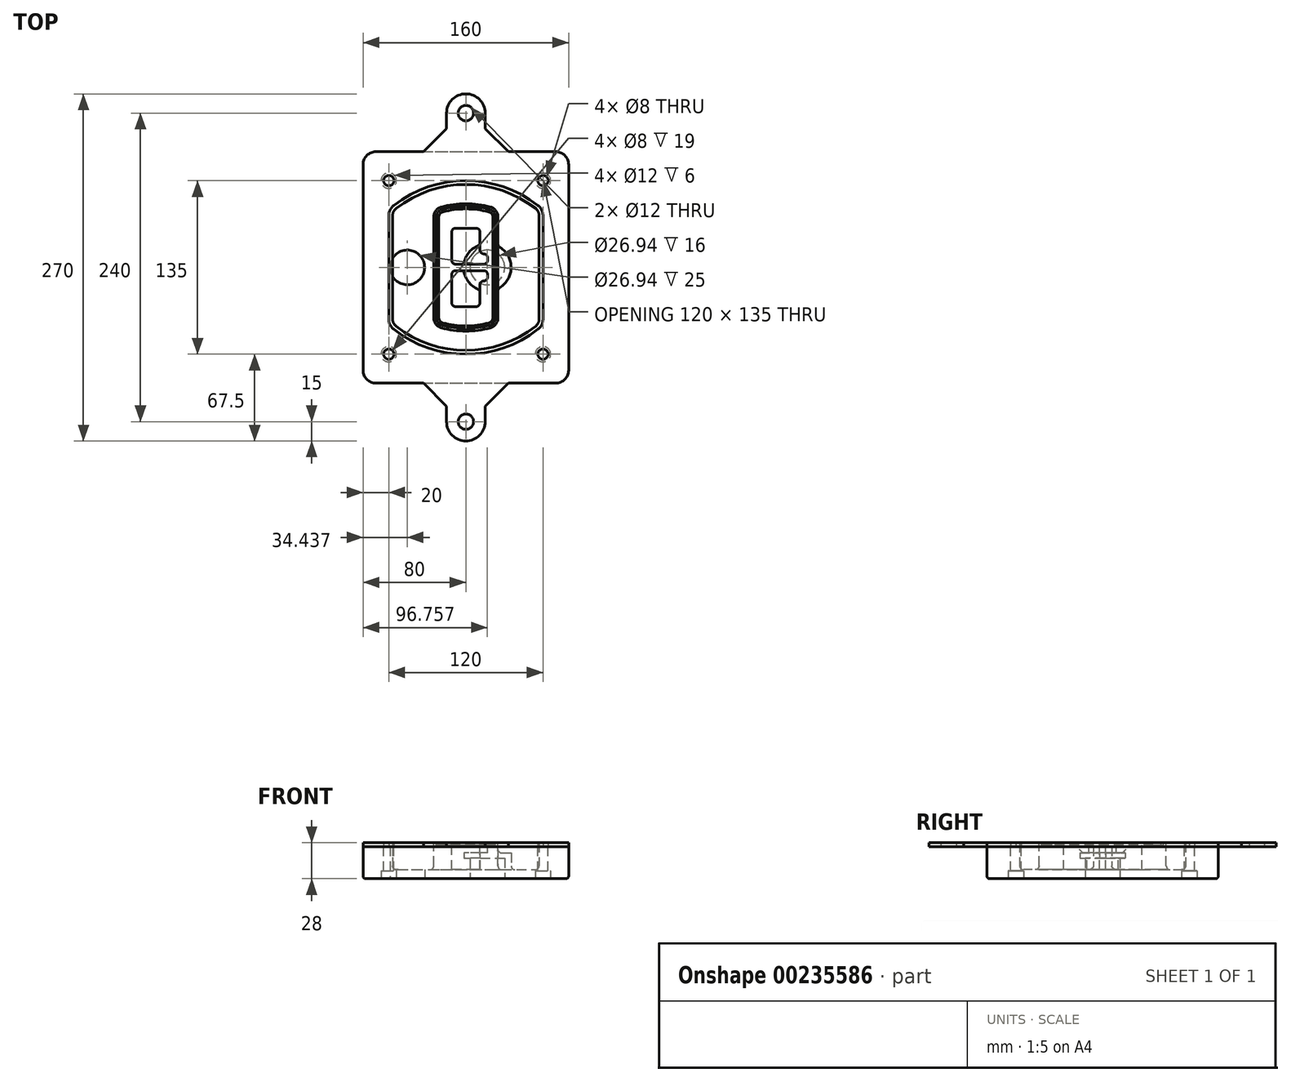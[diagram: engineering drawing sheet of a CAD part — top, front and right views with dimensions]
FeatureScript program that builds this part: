
annotation { "Feature Type Name" : "Feature", "Feature Type Description" : "" }
export const myFeature = defineFeature(function(context is Context, id is Id, definition is map)
    precondition{}
    {
        {
            var Q0;
            Q0=qCreatedBy(makeId("Top.planeOp"),FACE);
            var sketch = newSketch(context, id + "F0", { "sketchPlane" : qUnion([Q0])});
            skPoint(sketch, "E0.rect.middle", {"position": v(0, 0) * mm});
            skLineSegment(sketch, "E1.bottom", {"start": v(-70, -90) * mm, "end": v(70, -90) * mm});
            skLineSegment(sketch, "E1.top", {"start": v(-70, 90) * mm, "end": v(70, 90) * mm});
            skLineSegment(sketch, "E1.left", {"start": v(-80, -80) * mm, "end": v(-80, 80) * mm});
            skLineSegment(sketch, "E1.right", {"start": v(80, -80) * mm, "end": v(80, 80) * mm});
            skLineSegment(sketch, "E2", {"start": v(-80, 90) * mm, "end": v(80, -90) * mm, "construction": true});
            skLineSegment(sketch, "E3", {"start": v(80, 90) * mm, "end": v(-80, -90) * mm, "construction": true});
            skCircle(sketch, "E4", {"center": v(-60, 67.5) * mm, "radius": 4 * mm});
            skCircle(sketch, "E5", {"center": v(60, 67.5) * mm, "radius": 4 * mm});
            skCircle(sketch, "E6", {"center": v(60, -67.5) * mm, "radius": 4 * mm});
            skCircle(sketch, "E7", {"center": v(-60, -67.5) * mm, "radius": 4 * mm});
            skLineSegment(sketch, "E8", {"start": v(-60, 67.5) * mm, "end": v(60, 67.5) * mm, "construction": true});
            skLineSegment(sketch, "E9", {"start": v(60, 67.5) * mm, "end": v(60, -67.5) * mm, "construction": true});
            skLineSegment(sketch, "E10", {"start": v(60, -67.5) * mm, "end": v(-60, -67.5) * mm, "construction": true});
            skLineSegment(sketch, "E11", {"start": v(-60, -67.5) * mm, "end": v(-60, 67.5) * mm, "construction": true});
            skLineSegment(sketch, "E12", {"start": v(-60, 40.3) * mm, "end": v(-60, -40.3) * mm});
            skLineSegment(sketch, "E13", {"start": v(60, 40.3) * mm, "end": v(60, -40.3) * mm});
            skArc(sketch, "E14", {"start": v(56.15, 48.18) * mm, "mid": v(0, 67.5) * mm, "end": v(-56.15, 48.18) * mm});
            skArc(sketch, "E15", {"start": v(-56.15, -48.18) * mm, "mid": v(0, -67.5) * mm, "end": v(56.15, -48.18) * mm});
            skLineSegment(sketch, "E16", {"start": v(-60, 0) * mm, "end": v(60, 0) * mm, "construction": true});
            skPoint(sketch, "E17.visualSharp", {"position": v(-60, -45) * mm});
            skArc(sketch, "E17.filletArc", {"start": v(-60, -40.3) * mm, "mid": v(-58.99, -44.68) * mm, "end": v(-56.15, -48.18) * mm});
            skPoint(sketch, "E18.visualSharp", {"position": v(-60, 45) * mm});
            skArc(sketch, "E18.filletArc", {"start": v(-56.15, 48.18) * mm, "mid": v(-58.99, 44.68) * mm, "end": v(-60, 40.3) * mm});
            skPoint(sketch, "E19.visualSharp", {"position": v(60, 45) * mm});
            skArc(sketch, "E19.filletArc", {"start": v(60, 40.3) * mm, "mid": v(58.99, 44.68) * mm, "end": v(56.15, 48.18) * mm});
            skPoint(sketch, "E20.visualSharp", {"position": v(60, -45) * mm});
            skArc(sketch, "E20.filletArc", {"start": v(56.15, -48.18) * mm, "mid": v(58.99, -44.68) * mm, "end": v(60, -40.3) * mm});
            skPoint(sketch, "E21.visualSharp", {"position": v(-80, 90) * mm});
            skArc(sketch, "E21.filletArc", {"start": v(-70, 90) * mm, "mid": v(-77.07, 87.07) * mm, "end": v(-80, 80) * mm});
            skPoint(sketch, "E22.visualSharp", {"position": v(80, 90) * mm});
            skArc(sketch, "E22.filletArc", {"start": v(80, 80) * mm, "mid": v(77.07, 87.07) * mm, "end": v(70, 90) * mm});
            skPoint(sketch, "E23.visualSharp", {"position": v(80, -90) * mm});
            skArc(sketch, "E23.filletArc", {"start": v(70, -90) * mm, "mid": v(77.07, -87.07) * mm, "end": v(80, -80) * mm});
            skPoint(sketch, "E24.visualSharp", {"position": v(-80, -90) * mm});
            skArc(sketch, "E24.filletArc", {"start": v(-80, -80) * mm, "mid": v(-77.07, -87.07) * mm, "end": v(-70, -90) * mm});
            skArc(sketch, "E25.0", {"start": v(57, 40.3) * mm, "mid": v(56.3, 43.36) * mm, "end": v(54.3, 45.81) * mm});
            skLineSegment(sketch, "E25.1", {"start": v(57, 40.3) * mm, "end": v(57, -40.3) * mm});
            skArc(sketch, "E25.2", {"start": v(54.3, -45.81) * mm, "mid": v(56.3, -43.36) * mm, "end": v(57, -40.3) * mm});
            skArc(sketch, "E25.3", {"start": v(-54.3, -45.81) * mm, "mid": v(0, -64.5) * mm, "end": v(54.3, -45.81) * mm});
            skArc(sketch, "E25.4", {"start": v(-57, -40.3) * mm, "mid": v(-56.3, -43.36) * mm, "end": v(-54.3, -45.81) * mm});
            skArc(sketch, "E25.5", {"start": v(54.3, 45.81) * mm, "mid": v(0, 64.5) * mm, "end": v(-54.3, 45.81) * mm});
            skLineSegment(sketch, "E25.6", {"start": v(-57, 40.3) * mm, "end": v(-57, -40.3) * mm});
            skArc(sketch, "E25.7", {"start": v(-54.3, 45.81) * mm, "mid": v(-56.3, 43.36) * mm, "end": v(-57, 40.3) * mm});
            skArc(sketch, "E26.0", {"start": v(-58.62, 51.33) * mm, "mid": v(-62.58, 46.43) * mm, "end": v(-64, 40.3) * mm});
            skArc(sketch, "E26.1", {"start": v(58.62, 51.33) * mm, "mid": v(0, 71.5) * mm, "end": v(-58.62, 51.33) * mm});
            skArc(sketch, "E26.2", {"start": v(64, 40.3) * mm, "mid": v(62.58, 46.43) * mm, "end": v(58.62, 51.33) * mm});
            skLineSegment(sketch, "E26.3", {"start": v(64, 40.3) * mm, "end": v(64, -40.3) * mm});
            skArc(sketch, "E26.4", {"start": v(58.62, -51.33) * mm, "mid": v(62.58, -46.43) * mm, "end": v(64, -40.3) * mm});
            skLineSegment(sketch, "E26.5", {"start": v(-64, 40.3) * mm, "end": v(-64, -40.3) * mm});
            skArc(sketch, "E26.6", {"start": v(-58.62, -51.33) * mm, "mid": v(0, -71.5) * mm, "end": v(58.62, -51.33) * mm});
            skArc(sketch, "E26.7", {"start": v(-64, -40.3) * mm, "mid": v(-62.58, -46.43) * mm, "end": v(-58.62, -51.33) * mm});
            skSolve(sketch);
        }
        {
            var Q0;
            Q0=makeQuery(id+"F0.imprint","IMPRINT",FACE,{"disambiguationData":[TD([[makeQuery(id+"F0.imprint","IMPRINT",EDGE,{"derivedFrom":sQuery(id+"F0.wireOp",EDGE,"E1.bottom")}),1.0]])]});
            var Q1;
            Q1=makeQuery(id+"F0.imprint","IMPRINT",FACE,{"disambiguationData":[TD([[makeQuery(id+"F0.imprint","IMPRINT",EDGE,{"derivedFrom":sQuery(id+"F0.wireOp",EDGE,"E12")}),1.0]])]});
            var Q2;
            Q2=makeQuery(id+"F0.imprint","IMPRINT",FACE,{"disambiguationData":[TD([[makeQuery(id+"F0.imprint","IMPRINT",EDGE,{"derivedFrom":sQuery(id+"F0.wireOp",EDGE,"E25.0")}),1.0]])]});
            var Q3;
            Q3=makeQuery(id+"F0.imprint","IMPRINT",FACE,{"disambiguationData":[TD([[makeQuery(id+"F0.imprint","IMPRINT",EDGE,{"derivedFrom":sQuery(id+"F0.wireOp",EDGE,"E12")}),-1.0]])]});
            extrude(context, id + "F1", {"entities" : qUnion([Q0, Q1, Q2, Q3]), "oppositeDirection" : true, "depth" : 25 * mm});
        }
        {
            var Q0;
            Q0=makeQuery(id+"F0.imprint","IMPRINT",FACE,{"disambiguationData":[TD([[makeQuery(id+"F0.imprint","IMPRINT",EDGE,{"derivedFrom":sQuery(id+"F0.wireOp",EDGE,"E12")}),1.0]])]});
            extrude(context, id + "F2", {"entities" : qUnion([Q0]), "operationType" : NewBodyOperationType.ADD, "depth" : 3 * mm});
        }
        {
            var Q0;
            Q0=makeQuery(id+"F0.imprint","IMPRINT",FACE,{"disambiguationData":[TD([[makeQuery(id+"F0.imprint","IMPRINT",EDGE,{"derivedFrom":sQuery(id+"F0.wireOp",EDGE,"E25.0")}),1.0]])]});
            extrude(context, id + "F3", {"entities" : qUnion([Q0]), "operationType" : NewBodyOperationType.REMOVE, "oppositeDirection" : true, "depth" : 18 * mm});
        }
        {
            var Q0;
            Q0=makeQuery(id+"F2.opExtrude","CAP_FACE",FACE,{"disambiguationData":[OSD([sQuery(id+"F0.wireOp",EDGE,"E12"),sQuery(id+"F0.wireOp",EDGE,"E13"),sQuery(id+"F0.wireOp",EDGE,"E14"),sQuery(id+"F0.wireOp",EDGE,"E15"),sQuery(id+"F0.wireOp",EDGE,"E17.filletArc"),sQuery(id+"F0.wireOp",EDGE,"E18.filletArc"),sQuery(id+"F0.wireOp",EDGE,"E19.filletArc"),sQuery(id+"F0.wireOp",EDGE,"E20.filletArc"),sQuery(id+"F0.wireOp",EDGE,"E25.0"),sQuery(id+"F0.wireOp",EDGE,"E25.1"),sQuery(id+"F0.wireOp",EDGE,"E25.2"),sQuery(id+"F0.wireOp",EDGE,"E25.3"),sQuery(id+"F0.wireOp",EDGE,"E25.4"),sQuery(id+"F0.wireOp",EDGE,"E25.5"),sQuery(id+"F0.wireOp",EDGE,"E25.6"),sQuery(id+"F0.wireOp",EDGE,"E25.7")])],"isStart":false});
            var sketch = newSketch(context, id + "F4", { "sketchPlane" : qUnion([Q0])});
            skArc(sketch, "E27.0", {"start": v(-19.08, -46.97) * mm, "mid": v(0, -49.5) * mm, "end": v(19.08, -46.97) * mm});
            skArc(sketch, "E28.0", {"start": v(19.08, 46.97) * mm, "mid": v(0, 49.5) * mm, "end": v(-19.08, 46.97) * mm});
            skLineSegment(sketch, "E29", {"start": v(-25, 39.25) * mm, "end": v(-25, -39.25) * mm});
            skLineSegment(sketch, "E30", {"start": v(25, 39.25) * mm, "end": v(25, -39.25) * mm});
            skLineSegment(sketch, "E31", {"start": v(-25, 45.1) * mm, "end": v(25, 45.1) * mm, "construction": true});
            skLineSegment(sketch, "E32", {"start": v(-25, -45.1) * mm, "end": v(25, -45.1) * mm, "construction": true});
            skPoint(sketch, "E33.visualSharp", {"position": v(-25, 45.1) * mm});
            skArc(sketch, "E33.filletArc", {"start": v(-19.08, 46.97) * mm, "mid": v(-23.35, 44.11) * mm, "end": v(-25, 39.25) * mm});
            skPoint(sketch, "E34.visualSharp", {"position": v(25, 45.1) * mm});
            skArc(sketch, "E34.filletArc", {"start": v(25, 39.25) * mm, "mid": v(23.35, 44.11) * mm, "end": v(19.08, 46.97) * mm});
            skPoint(sketch, "E35.visualSharp", {"position": v(25, -45.1) * mm});
            skArc(sketch, "E35.filletArc", {"start": v(19.08, -46.97) * mm, "mid": v(23.35, -44.11) * mm, "end": v(25, -39.25) * mm});
            skPoint(sketch, "E36.visualSharp", {"position": v(-25, -45.1) * mm});
            skArc(sketch, "E36.filletArc", {"start": v(-25, -39.25) * mm, "mid": v(-23.35, -44.11) * mm, "end": v(-19.08, -46.97) * mm});
            skArc(sketch, "E37.0", {"start": v(54.3, 45.81) * mm, "mid": v(0, 64.5) * mm, "end": v(-54.3, 45.81) * mm});
            skArc(sketch, "E37.1", {"start": v(-54.3, 45.81) * mm, "mid": v(-56.3, 43.36) * mm, "end": v(-57, 40.3) * mm});
            skLineSegment(sketch, "E37.2", {"start": v(-57, 40.3) * mm, "end": v(-57, -40.3) * mm});
            skArc(sketch, "E37.3", {"start": v(-57, -40.3) * mm, "mid": v(-56.3, -43.36) * mm, "end": v(-54.3, -45.81) * mm});
            skArc(sketch, "E37.4", {"start": v(-54.3, -45.81) * mm, "mid": v(0, -64.5) * mm, "end": v(54.3, -45.81) * mm});
            skArc(sketch, "E37.5", {"start": v(54.3, -45.81) * mm, "mid": v(56.3, -43.36) * mm, "end": v(57, -40.3) * mm});
            skLineSegment(sketch, "E37.6", {"start": v(57, 40.3) * mm, "end": v(57, -40.3) * mm});
            skArc(sketch, "E37.7", {"start": v(57, 40.3) * mm, "mid": v(56.3, 43.36) * mm, "end": v(54.3, 45.81) * mm});
            skLineSegment(sketch, "E38.0", {"start": v(23, 39.25) * mm, "end": v(23, -39.25) * mm});
            skArc(sketch, "E38.1", {"start": v(18.56, -45.04) * mm, "mid": v(21.76, -42.9) * mm, "end": v(23, -39.25) * mm});
            skArc(sketch, "E38.2", {"start": v(-18.56, -45.04) * mm, "mid": v(0, -47.5) * mm, "end": v(18.56, -45.04) * mm});
            skArc(sketch, "E38.3", {"start": v(-23, -39.25) * mm, "mid": v(-21.76, -42.9) * mm, "end": v(-18.56, -45.04) * mm});
            skLineSegment(sketch, "E38.4", {"start": v(-23, 39.25) * mm, "end": v(-23, -39.25) * mm});
            skArc(sketch, "E38.5", {"start": v(23, 39.25) * mm, "mid": v(21.76, 42.9) * mm, "end": v(18.56, 45.04) * mm});
            skArc(sketch, "E38.6", {"start": v(-18.56, 45.04) * mm, "mid": v(-21.76, 42.9) * mm, "end": v(-23, 39.25) * mm});
            skArc(sketch, "E38.7", {"start": v(18.56, 45.04) * mm, "mid": v(0, 47.5) * mm, "end": v(-18.56, 45.04) * mm});
            skArc(sketch, "E39.0", {"start": v(21, 39.25) * mm, "mid": v(20.18, 41.68) * mm, "end": v(18.04, 43.1) * mm});
            skLineSegment(sketch, "E39.1", {"start": v(21, 39.25) * mm, "end": v(21, -39.25) * mm});
            skArc(sketch, "E39.2", {"start": v(18.04, -43.1) * mm, "mid": v(20.18, -41.68) * mm, "end": v(21, -39.25) * mm});
            skArc(sketch, "E39.3", {"start": v(-18.04, -43.1) * mm, "mid": v(0, -45.5) * mm, "end": v(18.04, -43.1) * mm});
            skArc(sketch, "E39.4", {"start": v(-21, -39.25) * mm, "mid": v(-20.18, -41.68) * mm, "end": v(-18.04, -43.1) * mm});
            skArc(sketch, "E39.5", {"start": v(18.04, 43.1) * mm, "mid": v(0, 45.5) * mm, "end": v(-18.04, 43.1) * mm});
            skLineSegment(sketch, "E39.6", {"start": v(-21, 39.25) * mm, "end": v(-21, -39.25) * mm});
            skArc(sketch, "E39.7", {"start": v(-18.04, 43.1) * mm, "mid": v(-20.18, 41.68) * mm, "end": v(-21, 39.25) * mm});
            skLineSegment(sketch, "E40", {"start": v(-25, 0) * mm, "end": v(25, 0) * mm, "construction": true});
            skLineSegment(sketch, "E41", {"start": v(-11, 5.5) * mm, "end": v(-11, 27.5) * mm});
            skLineSegment(sketch, "E42", {"start": v(-8, 30.5) * mm, "end": v(8, 30.5) * mm});
            skLineSegment(sketch, "E43", {"start": v(11, 27.5) * mm, "end": v(11, 13.5) * mm});
            skLineSegment(sketch, "E44", {"start": v(14, 10.5) * mm, "end": v(14, 10.5) * mm});
            skLineSegment(sketch, "E45", {"start": v(17, 7.5) * mm, "end": v(17, 5.5) * mm});
            skLineSegment(sketch, "E46", {"start": v(14, 2.5) * mm, "end": v(-8, 2.5) * mm});
            skPoint(sketch, "E47.visualSharp", {"position": v(-11, 30.5) * mm});
            skArc(sketch, "E47.filletArc", {"start": v(-8, 30.5) * mm, "mid": v(-10.12, 29.62) * mm, "end": v(-11, 27.5) * mm});
            skPoint(sketch, "E48.visualSharp", {"position": v(11, 30.5) * mm});
            skArc(sketch, "E48.filletArc", {"start": v(11, 27.5) * mm, "mid": v(10.12, 29.62) * mm, "end": v(8, 30.5) * mm});
            skPoint(sketch, "E49.visualSharp", {"position": v(11, 10.5) * mm});
            skArc(sketch, "E49.filletArc", {"start": v(11, 13.5) * mm, "mid": v(11.88, 11.38) * mm, "end": v(14, 10.5) * mm});
            skPoint(sketch, "E50.visualSharp", {"position": v(17, 10.5) * mm});
            skArc(sketch, "E50.filletArc", {"start": v(17, 7.5) * mm, "mid": v(16.12, 9.62) * mm, "end": v(14, 10.5) * mm});
            skPoint(sketch, "E51.visualSharp", {"position": v(17, 2.5) * mm});
            skArc(sketch, "E51.filletArc", {"start": v(14, 2.5) * mm, "mid": v(16.12, 3.38) * mm, "end": v(17, 5.5) * mm});
            skPoint(sketch, "E52.visualSharp", {"position": v(-11, 2.5) * mm});
            skArc(sketch, "E52.filletArc", {"start": v(-11, 5.5) * mm, "mid": v(-10.12, 3.38) * mm, "end": v(-8, 2.5) * mm});
            skLineSegment(sketch, "E53.0.MirrorCS", {"start": v(14, -2.5) * mm, "end": v(-8, -2.5) * mm});
            skArc(sketch, "E54.0.MirrorCS", {"start": v(-11, -5.5) * mm, "mid": v(-10.12, -3.38) * mm, "end": v(-8, -2.5) * mm});
            skLineSegment(sketch, "E55.0.MirrorCS", {"start": v(-11, -5.5) * mm, "end": v(-11, -27.5) * mm});
            skArc(sketch, "E56.0.MirrorCS", {"start": v(-8, -30.5) * mm, "mid": v(-10.12, -29.62) * mm, "end": v(-11, -27.5) * mm});
            skLineSegment(sketch, "E57.0.MirrorCS", {"start": v(-8, -30.5) * mm, "end": v(8, -30.5) * mm});
            skArc(sketch, "E58.0.MirrorCS", {"start": v(11, -27.5) * mm, "mid": v(10.12, -29.62) * mm, "end": v(8, -30.5) * mm});
            skLineSegment(sketch, "E59.0.MirrorCS", {"start": v(11, -27.5) * mm, "end": v(11, -13.5) * mm});
            skArc(sketch, "E60.0.MirrorCS", {"start": v(11, -13.5) * mm, "mid": v(11.88, -11.38) * mm, "end": v(14, -10.5) * mm});
            skArc(sketch, "E61.0.MirrorCS", {"start": v(17, -7.5) * mm, "mid": v(16.12, -9.62) * mm, "end": v(14, -10.5) * mm});
            skLineSegment(sketch, "E62.0.MirrorCS", {"start": v(17, -7.5) * mm, "end": v(17, -5.5) * mm});
            skArc(sketch, "E63.0.MirrorCS", {"start": v(14, -2.5) * mm, "mid": v(16.12, -3.38) * mm, "end": v(17, -5.5) * mm});
            skSolve(sketch);
        }
        {
            var Q0;
            Q0=makeQuery(id+"F4.imprint","IMPRINT",FACE,{"disambiguationData":[TD([[makeQuery(id+"F4.imprint","IMPRINT",EDGE,{"derivedFrom":sQuery(id+"F4.wireOp",EDGE,"E27.0")}),1.0]])]});
            var Q1;
            Q1=makeQuery(id+"F4.imprint","IMPRINT",FACE,{"disambiguationData":[TD([[makeQuery(id+"F4.imprint","IMPRINT",EDGE,{"derivedFrom":sQuery(id+"F4.wireOp",EDGE,"E38.0")}),-1.0]])]});
            var Q2;
            Q2=makeQuery(id+"F4.imprint","IMPRINT",FACE,{"disambiguationData":[TD([[makeQuery(id+"F4.imprint","IMPRINT",EDGE,{"derivedFrom":sQuery(id+"F4.wireOp",EDGE,"E39.0")}),1.0]])]});
            extrude(context, id + "F5", {"entities" : qUnion([Q0, Q1, Q2]), "operationType" : NewBodyOperationType.ADD, "endBound" : BoundingType.UP_TO_NEXT, "oppositeDirection" : true, "depth" : 25 * mm});
        }
        {
            var Q0;
            Q0=makeQuery(id+"F4.imprint","IMPRINT",FACE,{"disambiguationData":[TD([[makeQuery(id+"F4.imprint","IMPRINT",EDGE,{"derivedFrom":sQuery(id+"F4.wireOp",EDGE,"E38.0")}),-1.0]])]});
            extrude(context, id + "F6", {"entities" : qUnion([Q0]), "operationType" : NewBodyOperationType.REMOVE, "oppositeDirection" : true, "depth" : 2 * mm});
        }
        {
            var Q0;
            Q0=makeQuery(id+"F1.opExtrude","CAP_FACE",FACE,{"disambiguationData":[OSD([sQuery(id+"F0.wireOp",EDGE,"E1.bottom"),sQuery(id+"F0.wireOp",EDGE,"E1.top"),sQuery(id+"F0.wireOp",EDGE,"E1.left"),sQuery(id+"F0.wireOp",EDGE,"E1.right"),sQuery(id+"F0.wireOp",EDGE,"E4"),sQuery(id+"F0.wireOp",EDGE,"E5"),sQuery(id+"F0.wireOp",EDGE,"E6"),sQuery(id+"F0.wireOp",EDGE,"E7"),sQuery(id+"F0.wireOp",EDGE,"E21.filletArc"),sQuery(id+"F0.wireOp",EDGE,"E22.filletArc"),sQuery(id+"F0.wireOp",EDGE,"E23.filletArc"),sQuery(id+"F0.wireOp",EDGE,"E24.filletArc")])],"isStart":false});
            var sketch = newSketch(context, id + "F7", { "sketchPlane" : qUnion([Q0])});
            skCircle(sketch, "E64", {"center": v(16.76, 0) * mm, "radius": 13.47 * mm});
            skCircle(sketch, "E65", {"center": v(-45.56, 0) * mm, "radius": 13.47 * mm});
            skLineSegment(sketch, "E66", {"start": v(80, 0) * mm, "end": v(-80, 0) * mm});
            skCircle(sketch, "E67", {"center": v(16.76, 0) * mm, "radius": 18.47 * mm});
            skCircle(sketch, "E68", {"center": v(60, -67.5) * mm, "radius": 6 * mm});
            skCircle(sketch, "E69", {"center": v(-60, -67.5) * mm, "radius": 6 * mm});
            skCircle(sketch, "E70", {"center": v(-60, 67.5) * mm, "radius": 6 * mm});
            skCircle(sketch, "E71", {"center": v(60, 67.5) * mm, "radius": 6 * mm});
            skSolve(sketch);
        }
        {
            var Q0;
            {var subQ1=sQuery(id+"F7.wireOp",EDGE,"E66");var subQ4=sQuery(id+"F7.wireOp",EDGE,"E64");var subQ6=makeQuery(id+"F7.imprint","INTERSECT",VERTEX,{"disambiguationData":[OD(0.0)],"derivedFrom":[subQ4,subQ1]});Q0=makeQuery(id+"F7.imprint","IMPRINT",FACE,{"disambiguationData":[TD([[makeQuery(id+"F7.imprint","IMPRINT",EDGE,{"disambiguationData":[TD([[subQ6,-1.0]])],"derivedFrom":subQ4}),-1.0]])]});}
            var Q1;
            {var subQ0=sQuery(id+"F7.wireOp",EDGE,"E66");var subQ1=sQuery(id+"F7.wireOp",EDGE,"E64");var subQ3=makeQuery(id+"F7.imprint","INTERSECT",VERTEX,{"disambiguationData":[OD(0.0)],"derivedFrom":[subQ1,subQ0]});Q1=makeQuery(id+"F7.imprint","IMPRINT",FACE,{"disambiguationData":[TD([[makeQuery(id+"F7.imprint","IMPRINT",EDGE,{"disambiguationData":[TD([[subQ3,-1.0]])],"derivedFrom":subQ1}),1.0]])]});}
            var Q2;
            {var subQ0=sQuery(id+"F7.wireOp",EDGE,"E66");var subQ1=sQuery(id+"F7.wireOp",EDGE,"E64");var subQ3=makeQuery(id+"F7.imprint","INTERSECT",VERTEX,{"disambiguationData":[OD(0.0)],"derivedFrom":[subQ1,subQ0]});Q2=makeQuery(id+"F7.imprint","IMPRINT",FACE,{"disambiguationData":[TD([[makeQuery(id+"F7.imprint","IMPRINT",EDGE,{"disambiguationData":[TD([[subQ3,1.0]])],"derivedFrom":subQ1}),1.0]])]});}
            var Q3;
            {var subQ1=sQuery(id+"F7.wireOp",EDGE,"E66");var subQ4=sQuery(id+"F7.wireOp",EDGE,"E64");var subQ6=makeQuery(id+"F7.imprint","INTERSECT",VERTEX,{"disambiguationData":[OD(0.0)],"derivedFrom":[subQ4,subQ1]});Q3=makeQuery(id+"F7.imprint","IMPRINT",FACE,{"disambiguationData":[TD([[makeQuery(id+"F7.imprint","IMPRINT",EDGE,{"disambiguationData":[TD([[subQ6,1.0]])],"derivedFrom":subQ4}),-1.0]])]});}
            extrude(context, id + "F8", {"entities" : qUnion([Q0, Q1, Q2, Q3]), "operationType" : NewBodyOperationType.ADD, "oppositeDirection" : true, "depth" : 20 * mm});
        }
        {
            var Q0;
            {var subQ0=sQuery(id+"F7.wireOp",EDGE,"E66");var subQ1=sQuery(id+"F7.wireOp",EDGE,"E64");var subQ3=makeQuery(id+"F7.imprint","INTERSECT",VERTEX,{"disambiguationData":[OD(0.0)],"derivedFrom":[subQ1,subQ0]});Q0=makeQuery(id+"F7.imprint","IMPRINT",FACE,{"disambiguationData":[TD([[makeQuery(id+"F7.imprint","IMPRINT",EDGE,{"disambiguationData":[TD([[subQ3,-1.0]])],"derivedFrom":subQ1}),1.0]])]});}
            var Q1;
            {var subQ0=sQuery(id+"F7.wireOp",EDGE,"E66");var subQ1=sQuery(id+"F7.wireOp",EDGE,"E64");var subQ3=makeQuery(id+"F7.imprint","INTERSECT",VERTEX,{"disambiguationData":[OD(0.0)],"derivedFrom":[subQ1,subQ0]});Q1=makeQuery(id+"F7.imprint","IMPRINT",FACE,{"disambiguationData":[TD([[makeQuery(id+"F7.imprint","IMPRINT",EDGE,{"disambiguationData":[TD([[subQ3,1.0]])],"derivedFrom":subQ1}),1.0]])]});}
            extrude(context, id + "F9", {"entities" : qUnion([Q0, Q1]), "operationType" : NewBodyOperationType.REMOVE, "oppositeDirection" : true, "depth" : 16 * mm});
        }
        {
            var Q0;
            {var subQ0=sQuery(id+"F7.wireOp",EDGE,"E66");var subQ1=sQuery(id+"F7.wireOp",EDGE,"E65");var subQ3=makeQuery(id+"F7.imprint","INTERSECT",VERTEX,{"disambiguationData":[OD(0.0)],"derivedFrom":[subQ1,subQ0]});Q0=makeQuery(id+"F7.imprint","IMPRINT",FACE,{"disambiguationData":[TD([[makeQuery(id+"F7.imprint","IMPRINT",EDGE,{"disambiguationData":[TD([[subQ3,-1.0]])],"derivedFrom":subQ1}),1.0]])]});}
            var Q1;
            {var subQ0=sQuery(id+"F7.wireOp",EDGE,"E66");var subQ1=sQuery(id+"F7.wireOp",EDGE,"E65");var subQ3=makeQuery(id+"F7.imprint","INTERSECT",VERTEX,{"disambiguationData":[OD(0.0)],"derivedFrom":[subQ1,subQ0]});Q1=makeQuery(id+"F7.imprint","IMPRINT",FACE,{"disambiguationData":[TD([[makeQuery(id+"F7.imprint","IMPRINT",EDGE,{"disambiguationData":[TD([[subQ3,1.0]])],"derivedFrom":subQ1}),1.0]])]});}
            extrude(context, id + "F10", {"entities" : qUnion([Q0, Q1]), "operationType" : NewBodyOperationType.REMOVE, "oppositeDirection" : true, "depth" : 25 * mm});
        }
        {
            var Q0;
            Q0=makeQuery(id+"F7.imprint","IMPRINT",FACE,{"disambiguationData":[TD([[makeQuery(id+"F7.imprint","IMPRINT",EDGE,{"derivedFrom":sQuery(id+"F7.wireOp",EDGE,"E68")}),1.0]])]});
            var Q1;
            Q1=makeQuery(id+"F7.imprint","IMPRINT",FACE,{"disambiguationData":[TD([[makeQuery(id+"F7.imprint","IMPRINT",EDGE,{"derivedFrom":makeQuery(id+"F1.opExtrude","CAP_EDGE",EDGE,{"disambiguationData":[OSD([sQuery(id+"F0.wireOp",EDGE,"E5")])],"isStart":false})}),-1.0]])]});
            var Q2;
            Q2=makeQuery(id+"F7.imprint","IMPRINT",FACE,{"disambiguationData":[TD([[makeQuery(id+"F7.imprint","IMPRINT",EDGE,{"derivedFrom":sQuery(id+"F7.wireOp",EDGE,"E69")}),1.0]])]});
            var Q3;
            Q3=makeQuery(id+"F7.imprint","IMPRINT",FACE,{"disambiguationData":[TD([[makeQuery(id+"F7.imprint","IMPRINT",EDGE,{"derivedFrom":makeQuery(id+"F1.opExtrude","CAP_EDGE",EDGE,{"disambiguationData":[OSD([sQuery(id+"F0.wireOp",EDGE,"E4")])],"isStart":false})}),-1.0]])]});
            var Q4;
            Q4=makeQuery(id+"F7.imprint","IMPRINT",FACE,{"disambiguationData":[TD([[makeQuery(id+"F7.imprint","IMPRINT",EDGE,{"derivedFrom":sQuery(id+"F7.wireOp",EDGE,"E70")}),1.0]])]});
            var Q5;
            Q5=makeQuery(id+"F7.imprint","IMPRINT",FACE,{"disambiguationData":[TD([[makeQuery(id+"F7.imprint","IMPRINT",EDGE,{"derivedFrom":makeQuery(id+"F1.opExtrude","CAP_EDGE",EDGE,{"disambiguationData":[OSD([sQuery(id+"F0.wireOp",EDGE,"E7")])],"isStart":false})}),-1.0]])]});
            var Q6;
            Q6=makeQuery(id+"F7.imprint","IMPRINT",FACE,{"disambiguationData":[TD([[makeQuery(id+"F7.imprint","IMPRINT",EDGE,{"derivedFrom":sQuery(id+"F7.wireOp",EDGE,"E71")}),1.0]])]});
            var Q7;
            Q7=makeQuery(id+"F7.imprint","IMPRINT",FACE,{"disambiguationData":[TD([[makeQuery(id+"F7.imprint","IMPRINT",EDGE,{"derivedFrom":makeQuery(id+"F1.opExtrude","CAP_EDGE",EDGE,{"disambiguationData":[OSD([sQuery(id+"F0.wireOp",EDGE,"E6")])],"isStart":false})}),-1.0]])]});
            extrude(context, id + "F11", {"entities" : qUnion([Q0, Q1, Q2, Q3, Q4, Q5, Q6, Q7]), "operationType" : NewBodyOperationType.REMOVE, "oppositeDirection" : true, "depth" : 6 * mm});
        }
        {
            var Q0;
            Q0=makeQuery(id+"F9.boolean.opBoolean","COPY",FACE,{"derivedFrom":makeQuery(id+"F9.opExtrude","CAP_FACE",FACE,{"disambiguationData":[OSD([sQuery(id+"F7.wireOp",EDGE,"E64")])],"isStart":false})});
            var sketch = newSketch(context, id + "F12", { "sketchPlane" : qUnion([Q0])});
            skArc(sketch, "E72.0", {"start": v(11, 17.55) * mm, "mid": v(2.57, 11.82) * mm, "end": v(-1.54, 2.5) * mm});
            skArc(sketch, "E72.1", {"start": v(-1.54, -2.5) * mm, "mid": v(2.57, -11.82) * mm, "end": v(11, -17.55) * mm});
            skLineSegment(sketch, "E73", {"start": v(-1.54, -2.5) * mm, "end": v(14, -2.5) * mm});
            skLineSegment(sketch, "E74.0", {"start": v(14, 2.5) * mm, "end": v(-1.54, 2.5) * mm});
            skArc(sketch, "E74.1", {"start": v(14, 2.5) * mm, "mid": v(16.12, 3.38) * mm, "end": v(17, 5.5) * mm});
            skLineSegment(sketch, "E74.2", {"start": v(17, 7.5) * mm, "end": v(17, 5.5) * mm});
            skArc(sketch, "E74.3", {"start": v(17, 7.5) * mm, "mid": v(16.12, 9.62) * mm, "end": v(14, 10.5) * mm});
            skArc(sketch, "E74.4", {"start": v(11, 13.5) * mm, "mid": v(11.88, 11.38) * mm, "end": v(14, 10.5) * mm});
            skLineSegment(sketch, "E74.5", {"start": v(11, 17.55) * mm, "end": v(11, 13.5) * mm});
            skLineSegment(sketch, "E74.7", {"start": v(14, -2.5) * mm, "end": v(-1.54, -2.5) * mm});
            skArc(sketch, "E74.8", {"start": v(14, -2.5) * mm, "mid": v(16.12, -3.38) * mm, "end": v(17, -5.5) * mm});
            skLineSegment(sketch, "E74.9", {"start": v(17, -7.5) * mm, "end": v(17, -5.5) * mm});
            skArc(sketch, "E74.10", {"start": v(17, -7.5) * mm, "mid": v(16.12, -9.62) * mm, "end": v(14, -10.5) * mm});
            skArc(sketch, "E74.11", {"start": v(11, -13.5) * mm, "mid": v(11.88, -11.38) * mm, "end": v(14, -10.5) * mm});
            skLineSegment(sketch, "E74.12", {"start": v(11, -17.55) * mm, "end": v(11, -13.5) * mm});
            skPoint(sketch, "E75.orphan", {"position": v(11, -27.5) * mm});
            skPoint(sketch, "E76.orphan", {"position": v(-8, -2.5) * mm});
            skPoint(sketch, "E77.orphan", {"position": v(-8, 2.5) * mm});
            skPoint(sketch, "E78.orphan", {"position": v(11, 27.5) * mm});
            skSolve(sketch);
        }
        {
            var Q0;
            {var subQ7=sQuery(id+"F12.wireOp",EDGE,"E72.0");var subQ14=sQuery(id+"F12.wireOp",EDGE,"E72.1");var subQ16=sQuery(id+"F12.wireOp",EDGE,"E74.1");var subQ18=sQuery(id+"F12.wireOp",EDGE,"E74.8");Q0=qUnion([makeQuery(id+"F12.imprint","IMPRINT",FACE,{"disambiguationData":[TD([[makeQuery(id+"F12.imprint","IMPRINT",EDGE,{"derivedFrom":subQ7}),1.0]])]}),makeQuery(id+"F12.imprint","IMPRINT",FACE,{"disambiguationData":[TD([[makeQuery(id+"F12.imprint","IMPRINT",EDGE,{"derivedFrom":subQ14}),1.0]])]}),makeQuery(id+"F12.imprint","IMPRINT",FACE,{"disambiguationData":[TD([[makeQuery(id+"F12.imprint","IMPRINT",EDGE,{"derivedFrom":subQ16}),1.0]])]}),makeQuery(id+"F12.imprint","IMPRINT",FACE,{"disambiguationData":[TD([[makeQuery(id+"F12.imprint","IMPRINT",EDGE,{"derivedFrom":subQ18}),-1.0]])]})]);}
            var Q1;
            Q1=makeQuery(id+"F5.boolean.opBoolean","SPLIT",FACE,{"disambiguationData":[TD([makeQuery(id+"F5.opExtrude","SWEPT_FACE",FACE,{"disambiguationData":[OSD([sQuery(id+"F4.wireOp",EDGE,"E41")])]})])],"derivedFrom":makeQuery(id+"F3.boolean.opBoolean","COPY",FACE,{"derivedFrom":makeQuery(id+"F3.opExtrude","CAP_FACE",FACE,{"disambiguationData":[OSD([sQuery(id+"F0.wireOp",EDGE,"E25.0"),sQuery(id+"F0.wireOp",EDGE,"E25.1"),sQuery(id+"F0.wireOp",EDGE,"E25.2"),sQuery(id+"F0.wireOp",EDGE,"E25.3"),sQuery(id+"F0.wireOp",EDGE,"E25.4"),sQuery(id+"F0.wireOp",EDGE,"E25.5"),sQuery(id+"F0.wireOp",EDGE,"E25.6"),sQuery(id+"F0.wireOp",EDGE,"E25.7")])],"isStart":false})})});
            extrude(context, id + "F13", {"entities" : qUnion([Q0]), "operationType" : NewBodyOperationType.REMOVE, "endBound" : BoundingType.UP_TO_SURFACE, "endBoundEntityFace" : qUnion([Q1]), "depth" : 25 * mm});
        }
        {
            var Q0;
            Q0=makeQuery(id+"F3.boolean.opBoolean","COPY",EDGE,{"derivedFrom":makeQuery(id+"F3.opExtrude","CAP_EDGE",EDGE,{"disambiguationData":[OSD([sQuery(id+"F0.wireOp",EDGE,"E25.6")])],"isStart":false})});
            var Q1;
            Q1=makeQuery(id+"F8.boolean.opBoolean","INTERSECT",EDGE,{"derivedFrom":[makeQuery(id+"F5.opExtrude","SWEPT_FACE",FACE,{"disambiguationData":[OSD([sQuery(id+"F4.wireOp",EDGE,"E30")])]}),makeQuery(id+"F8.opExtrude","CAP_FACE",FACE,{"disambiguationData":[OSD([sQuery(id+"F7.wireOp",EDGE,"E67")])],"isStart":false})]});
            var Q2;
            Q2=makeQuery(id+"F8.boolean.opBoolean","INTERSECT",EDGE,{"disambiguationData":[OD(1.0)],"derivedFrom":[makeQuery(id+"F5.opExtrude","SWEPT_FACE",FACE,{"disambiguationData":[OSD([sQuery(id+"F4.wireOp",EDGE,"E30")])]}),makeQuery(id+"F8.opExtrude","SWEPT_FACE",FACE,{"disambiguationData":[OSD([sQuery(id+"F7.wireOp",EDGE,"E67")])]})]});
            var Q3;
            {var subQ0=sQuery(id+"F4.wireOp",EDGE,"E30");Q3=makeQuery(id+"F8.boolean.opBoolean","SPLIT",EDGE,{"disambiguationData":[TD([makeQuery(id+"F5.opExtrude","SWEPT_FACE",FACE,{"disambiguationData":[OSD([sQuery(id+"F4.wireOp",EDGE,"E35.filletArc")])]})])],"derivedFrom":makeQuery(id+"F5.opExtrude","CAP_EDGE",EDGE,{"disambiguationData":[OSD([subQ0])],"isStart":false})});}
            var Q4;
            {var subQ0=sQuery(id+"F0.wireOp",EDGE,"E25.7");var subQ1=sQuery(id+"F0.wireOp",EDGE,"E25.1");var subQ2=sQuery(id+"F0.wireOp",EDGE,"E25.6");var subQ3=sQuery(id+"F0.wireOp",EDGE,"E25.5");var subQ4=sQuery(id+"F0.wireOp",EDGE,"E25.4");var subQ5=sQuery(id+"F0.wireOp",EDGE,"E25.0");var subQ6=sQuery(id+"F0.wireOp",EDGE,"E25.2");var subQ7=sQuery(id+"F0.wireOp",EDGE,"E25.3");Q4=makeQuery(id+"F8.boolean.opBoolean","INTERSECT",EDGE,{"derivedFrom":[makeQuery(id+"F5.boolean.opBoolean","SPLIT",FACE,{"disambiguationData":[TD([makeQuery(id+"F2.opExtrude","SWEPT_FACE",FACE,{"disambiguationData":[OSD([subQ5])]})])],"derivedFrom":makeQuery(id+"F3.boolean.opBoolean","COPY",FACE,{"derivedFrom":makeQuery(id+"F3.opExtrude","CAP_FACE",FACE,{"disambiguationData":[OSD([subQ5,subQ1,subQ6,subQ7,subQ4,subQ3,subQ2,subQ0])],"isStart":false})})}),makeQuery(id+"F8.opExtrude","SWEPT_FACE",FACE,{"disambiguationData":[OSD([sQuery(id+"F7.wireOp",EDGE,"E67")])]})]});}
            var Q5;
            Q5=makeQuery(id+"F8.boolean.opBoolean","INTERSECT",EDGE,{"disambiguationData":[OD(0.0)],"derivedFrom":[makeQuery(id+"F5.opExtrude","SWEPT_FACE",FACE,{"disambiguationData":[OSD([sQuery(id+"F4.wireOp",EDGE,"E30")])]}),makeQuery(id+"F8.opExtrude","SWEPT_FACE",FACE,{"disambiguationData":[OSD([sQuery(id+"F7.wireOp",EDGE,"E67")])]})]});
            fillet(context, id + "F14", {"entities" : qUnion([Q0, Q1, Q2, Q3, Q4, Q5]), "radius" : 3 * mm, "tangentPropagation" : true, "allowEdgeOverflow" : false});
        }
        {
            var Q0;
            Q0=makeQuery(id+"F1.opExtrude","CAP_EDGE",EDGE,{"disambiguationData":[OSD([sQuery(id+"F0.wireOp",EDGE,"E1.bottom")])],"isStart":false});
            fillet(context, id + "F15", {"entities" : qUnion([Q0]), "radius" : 2 * mm, "tangentPropagation" : true, "allowEdgeOverflow" : false});
        }
        {
            var Q0;
            {var subQ0=sQuery(id+"F0.wireOp",EDGE,"E22.filletArc");var subQ1=sQuery(id+"F0.wireOp",EDGE,"E7");var subQ2=sQuery(id+"F0.wireOp",EDGE,"E6");var subQ3=sQuery(id+"F0.wireOp",EDGE,"E5");var subQ4=sQuery(id+"F0.wireOp",EDGE,"E4");var subQ5=sQuery(id+"F0.wireOp",EDGE,"E1.bottom");var subQ6=sQuery(id+"F0.wireOp",EDGE,"E21.filletArc");var subQ7=sQuery(id+"F0.wireOp",EDGE,"E1.top");var subQ8=sQuery(id+"F0.wireOp",EDGE,"E1.left");var subQ9=sQuery(id+"F0.wireOp",EDGE,"E1.right");var subQ10=sQuery(id+"F0.wireOp",EDGE,"E23.filletArc");var subQ11=sQuery(id+"F0.wireOp",EDGE,"E24.filletArc");Q0=makeQuery(id+"F2.boolean.opBoolean","SPLIT",FACE,{"disambiguationData":[TD([makeQuery(id+"F1.opExtrude","SWEPT_FACE",FACE,{"disambiguationData":[OSD([subQ5])]})])],"derivedFrom":makeQuery(id+"F1.opExtrude","CAP_FACE",FACE,{"disambiguationData":[OSD([subQ5,subQ7,subQ8,subQ9,subQ4,subQ3,subQ2,subQ1,subQ6,subQ0,subQ10,subQ11])],"isStart":true})});}
            var sketch = newSketch(context, id + "F16", { "sketchPlane" : qUnion([Q0])});
            skCircle(sketch, "E79", {"center": v(0, 120) * mm, "radius": 6 * mm});
            skArc(sketch, "E80", {"start": v(15, 120) * mm, "mid": v(0, 135) * mm, "end": v(-15, 120) * mm});
            skPoint(sketch, "E80.first.point", {"position": v(-15, 120) * mm});
            skPoint(sketch, "E80.second.point", {"position": v(0, 135) * mm});
            skPoint(sketch, "E80.third.point", {"position": v(15, 120) * mm});
            skLineSegment(sketch, "E81", {"start": v(-15, 120) * mm, "end": v(-15, 108) * mm});
            skLineSegment(sketch, "E82", {"start": v(15, 120) * mm, "end": v(15, 108) * mm});
            skLineSegment(sketch, "E83", {"start": v(-33, 90) * mm, "end": v(-15, 108) * mm});
            skLineSegment(sketch, "E84", {"start": v(15, 108) * mm, "end": v(33, 90) * mm});
            skLineSegment(sketch, "E85", {"start": v(-80, 0) * mm, "end": v(80, 0) * mm, "construction": true});
            skLineSegment(sketch, "E86.MirrorCS", {"start": v(-33, -90) * mm, "end": v(-15, -108) * mm});
            skLineSegment(sketch, "E87.MirrorCS", {"start": v(-15, -120) * mm, "end": v(-15, -108) * mm});
            skArc(sketch, "E88.MirrorCS", {"start": v(15, -120) * mm, "mid": v(0, -135) * mm, "end": v(-15, -120) * mm});
            skLineSegment(sketch, "E89.MirrorCS", {"start": v(15, -120) * mm, "end": v(15, -108) * mm});
            skLineSegment(sketch, "E90.MirrorCS", {"start": v(15, -108) * mm, "end": v(33, -90) * mm});
            skCircle(sketch, "E91.MirrorC", {"center": v(0, -120) * mm, "radius": 6 * mm});
            skLineSegment(sketch, "E92", {"start": v(0, 90) * mm, "end": v(0, 120) * mm, "construction": true});
            skLineSegment(sketch, "E93.MirrorCS", {"start": v(0, -90) * mm, "end": v(0, -120) * mm, "construction": true});
            skSolve(sketch);
        }
        {
            var Q0;
            Q0=makeQuery(id+"F16.imprint","IMPRINT",FACE,{"disambiguationData":[TD([[makeQuery(id+"F16.imprint","IMPRINT",EDGE,{"derivedFrom":sQuery(id+"F16.wireOp",EDGE,"E79")}),-1.0]])]});
            var Q1;
            {var subQ0=sQuery(id+"F16.wireOp",EDGE,"E86.MirrorCS");Q1=makeQuery(id+"F16.imprint","IMPRINT",FACE,{"disambiguationData":[TD([[makeQuery(id+"F16.imprint","IMPRINT",EDGE,{"derivedFrom":subQ0}),1.0]])]});}
            var Q2;
            Q2=makeQuery(id+"F16.imprint","IMPRINT",FACE,{"disambiguationData":[TD([[makeQuery(id+"F16.imprint","IMPRINT",EDGE,{"derivedFrom":makeQuery(id+"F1.opExtrude","CAP_EDGE",EDGE,{"disambiguationData":[OSD([sQuery(id+"F0.wireOp",EDGE,"E1.left")])],"isStart":true})}),-1.0]])]});
            var Q3;
            Q3=makeQuery(id+"F2.opExtrude","CAP_FACE",FACE,{"disambiguationData":[OSD([sQuery(id+"F0.wireOp",EDGE,"E12"),sQuery(id+"F0.wireOp",EDGE,"E13"),sQuery(id+"F0.wireOp",EDGE,"E14"),sQuery(id+"F0.wireOp",EDGE,"E15"),sQuery(id+"F0.wireOp",EDGE,"E17.filletArc"),sQuery(id+"F0.wireOp",EDGE,"E18.filletArc"),sQuery(id+"F0.wireOp",EDGE,"E19.filletArc"),sQuery(id+"F0.wireOp",EDGE,"E20.filletArc"),sQuery(id+"F0.wireOp",EDGE,"E25.0"),sQuery(id+"F0.wireOp",EDGE,"E25.1"),sQuery(id+"F0.wireOp",EDGE,"E25.2"),sQuery(id+"F0.wireOp",EDGE,"E25.3"),sQuery(id+"F0.wireOp",EDGE,"E25.4"),sQuery(id+"F0.wireOp",EDGE,"E25.5"),sQuery(id+"F0.wireOp",EDGE,"E25.6"),sQuery(id+"F0.wireOp",EDGE,"E25.7")])],"isStart":false});
            extrude(context, id + "F17", {"entities" : qUnion([Q0, Q1, Q2]), "endBound" : BoundingType.UP_TO_SURFACE, "endBoundEntityFace" : qUnion([Q3]), "depth" : 25 * mm});
        }
    });
